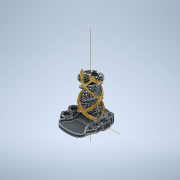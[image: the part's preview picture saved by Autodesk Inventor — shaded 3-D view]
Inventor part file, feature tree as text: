
AUTODESK INVENTOR PART (.ipt)
format: ipt  version: 2022 (Build 260153000, 153)  size: 7,762,432 bytes
history: native  units: mm
features: sketch x30, extrude x25, helix x5, plane x4, fillet x3, revolve x2, pattern_circular x2, chamfer x2
ambient origin geometry x8: Origin, YZ Plane, XZ Plane, XY Plane, X Axis, Y Axis, Z Axis, Center Point
bodies: Solid1 (feature_tree)
feature tree (73):
  revolve  "Revolution1"  [1 undecoded]
  plane  "Work Plane1"
  extrude  "Extrusion4"  Depth=20.0mm
  extrude  "Extrusion2"  Depth=19.0mm
  pattern_circular  "Circular Pattern2"  Count=9  [1 undecoded]
  plane  "Work Plane3"
  extrude  "Extrusion3"  Depth=10.0mm
  pattern_circular  "Circular Pattern3"  Count=7  [1 undecoded]
  helix  "Coil1"  [1 undecoded]
  helix  "Coil2"  [1 undecoded]
  helix  "Coil3"  [1 undecoded]
  helix  "Coil4"  [1 undecoded]
  helix  "Coil5"  [1 undecoded]
  extrude  "Extrusion5"  Depth=20.0mm
  revolve  "Revolution2"  [1 undecoded]
  extrude  "Extrusion6"  Depth=30.0mm
  extrude  "Extrusion15"  Depth=15.0mm
  extrude  "Extrusion16"  Depth=30.0mm
  extrude  "Extrusion17"  Depth=45.0mm
  extrude  "Extrusion18"  Depth=13.0mm
  extrude  "Extrusion19"  Depth=39.0mm
  extrude  "Extrusion20"  Depth=11.0mm
  extrude  "Extrusion21"  Depth=10.0mm
  extrude  "Extrusion22"  Depth=11.0mm
  extrude  "Extrusion23"  Depth=9.0mm
  extrude  "Extrusion25"  Depth=3.0mm TaperAngle=0.0deg
  extrude  "Extrusion26"  Depth=54.0mm TaperAngle=0.0deg
  extrude  "Extrusion27"  Depth=35.0mm
  extrude  "Extrusion28"  Depth=30.0mm
  extrude  "Extrusion29"  Depth=35.0mm
  extrude  "Extrusion30"  Depth=10.0mm TaperAngle=0.0deg
  extrude  "Extrusion31"  Depth=5.0mm TaperAngle=0.0deg
  plane  "Work Plane4"
  extrude  "Extrusion32"  Depth=10.0mm TaperAngle=0.0deg
  extrude  "Extrusion33"  Depth=15.0mm TaperAngle=0.0deg
  chamfer  "Chamfer2"  Distance=0.2mm
  chamfer  "Chamfer3"  Distance=5.0mm
  fillet  "Fillet5"  Radius=10.0mm
  fillet  "Fillet6"  Radius=15.0mm
  extrude  "Extrusion34"  Depth=3.0mm TaperAngle=0.0deg
  fillet  "Fillet16"  Radius=1.0mm
  extrude  "Extrusion35"  Depth=10.0mm TaperAngle=0.0deg
  sketch  "Sketch1"  dims[d11=50.0mm d12=40.0mm]
  sketch  "Sketch3"  dims[d13=20.0mm d14=20.0mm]
  plane  "Work Plane2"
  sketch  "Sketch4"  dims[d15=23.0mm d16=19.0mm d17=90.0mm]
  sketch  "Sketch5"  dims[d18=32.0mm d19=10.0mm]
  sketch  "Sketch7"  dims[d20=151.0mm]
  sketch  "Sketch8"  dims[d26=2.0mm]
  sketch  "Sketch9"  dims[d27=2.0mm]
  sketch  "Sketch10"  dims[d28=2.0mm]
  sketch  "Sketch11"  dims[d29=2.0mm]
  sketch  "Sketch13"  dims[d30=2.0mm]
  sketch  "Sketch16"  dims[d31=90.0deg d32=70.0mm d38=77.75mm d39=0.0mm d40=40.0mm d41=360.0deg d43=70.0mm d44=77.75mm d45=0.0mm d46=40.0mm d47=360.0deg]
  sketch  "Sketch17"  dims[d49=20.0mm d50=20.0mm]
  sketch  "Sketch20"  dims[d51=20.0mm d52=20.0mm]
  sketch  "Sketch21"  dims[d53=40.0mm d54=30.0mm]
  sketch  "Sketch22"  dims[d55=30.0mm d56=15.0mm]
  sketch  "Sketch23"  dims[d57=15.0mm d58=30.0mm]
  sketch  "Sketch26"  dims[d59=77.75mm d60=0.0mm d61=45.0mm]
  sketch  "Sketch27"  dims[d62=35.0mm]
  sketch  "Sketch28"  dims[d63=70.0mm d64=100.0mm d65=10.0mm d66=-0.567232mm d67=90.0deg d68=90.0deg d69=90.0deg d70=90.0deg d71=13.0mm]
  sketch  "Sketch30"  dims[d72=10.0mm d73=39.0mm]
  sketch  "Sketch31"  dims[d74=140.0mm d75=160.0mm d76=10.0mm d77=-0.645772mm d78=90.0deg d79=90.0deg d80=90.0deg d81=90.0deg d82=11.0mm]
  sketch  "Sketch33"  dims[d83=39.0mm d84=10.0mm]
  sketch  "Sketch35"  dims[d85=135.0mm d86=160.0mm d87=10.0mm d88=-0.645772mm d89=90.0deg d90=90.0deg d91=90.0deg d92=90.0deg d93=11.0mm]
  sketch  "Sketch37"  dims[d94=170.0mm d95=160.0mm d96=10.0mm d97=-0.645772mm d98=90.0deg d99=90.0deg d100=90.0deg d101=90.0deg d102=9.0mm]
  sketch  "Sketch38"  dims[d103=170.0mm d104=160.0mm d105=10.0mm d106=-0.645772mm d107=90.0deg d108=90.0deg d109=90.0deg d110=90.0deg d125=3.0mm d126=0.0mm]
  sketch  "Sketch39"  dims[d130=270.0deg d133=54.0mm d134=0.0mm]
  sketch  "Sketch40"  dims[d141=35.0mm d165=35.0mm]
  sketch  "Sketch41"  dims[d166=30.0mm d167=30.0mm d168=30.0mm d169=30.0mm]
  sketch  "Sketch43"  dims[d170=35.0mm d172=35.0mm]
  sketch  "Sketch44"  dims[d186=5.0mm d187=10.0mm d188=0.0mm d190=5.0mm d191=0.0mm d192=10.0mm d193=0.0mm d194=15.0mm d195=0.0mm d196=0.2mm d197=0.0mm d198=5.0mm d199=0.0mm d200=10.0mm d201=0.0mm d202=15.0mm d203=0.0mm d204=3.0mm d205=0.0mm d210=1.0mm d211=0.0mm d213=10.0mm d214=0.0mm d218=30.0mm d219=23.5mm d220=5.75mm d221=5.75mm d222=5.75mm d223=14.0mm d224=0.0mm d225=22.5mm d226=6.25mm d227=6.25mm d228=6.25mm d229=14.0mm d230=0.0mm d231=25.0mm d232=5.0mm d233=15.0mm d234=5.0mm d235=14.0mm d236=0.0mm d237=25.5mm d239=3.0mm d241=10.0mm d242=0.0mm d245=17.5mm d246=17.5mm d247=7.0mm d248=5.5mm d249=4.0mm d250=3.607976mm d251=10.0mm d252=0.0mm d253=21.0mm d254=21.0mm d255=5.0mm d256=4.0mm d257=5.0mm d258=24.0mm d259=0.0mm d263=25.0mm d266=5.0mm d267=5.0mm d268=12.0mm d269=0.0mm d270=11.0mm d271=2.0mm d272=45.0deg d273=12.0mm d274=2.0mm d275=45.0deg d276=35.0mm d277=3.0mm d278=5.0mm d279=5.0mm d280=5.0mm d282=2.0mm d283=1.56mm d292=20.0mm d293=0.0mm d295=2.0mm d299=25.0mm d300=52.0mm d301=54.0mm d302=0.0mm d132=0.0mm d135=0.0mm]
note: 9 required parameter values undecoded (feature->parameter linkage not recoverable at this tier; creation-order binding heuristic only, values carry confidence <= 0.55)